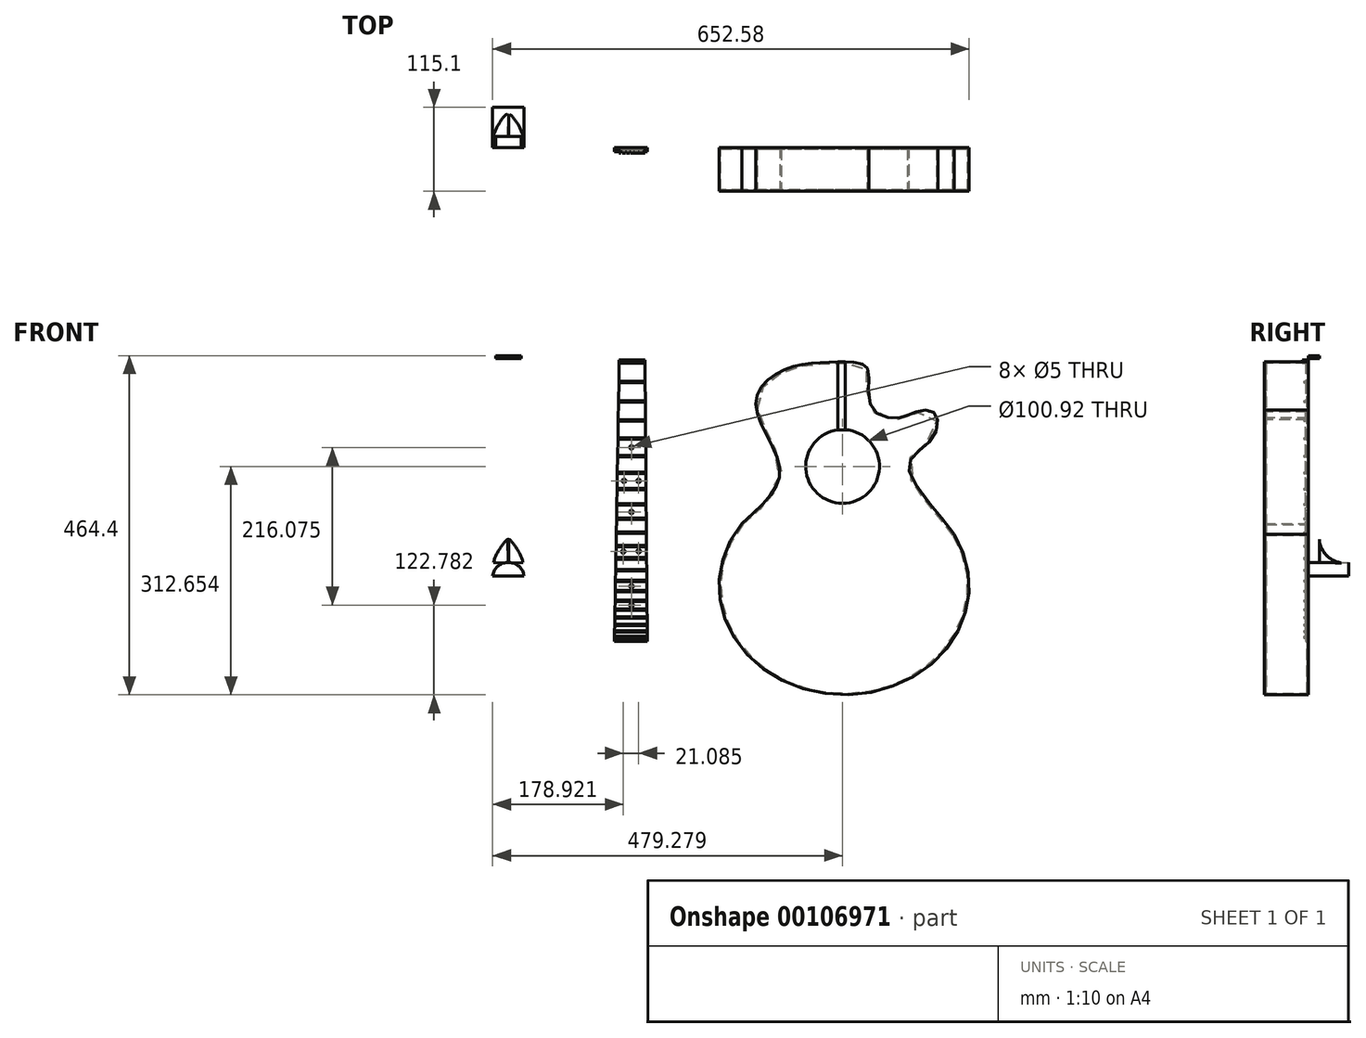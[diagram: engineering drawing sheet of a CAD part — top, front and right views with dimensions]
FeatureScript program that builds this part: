
annotation { "Feature Type Name" : "Feature", "Feature Type Description" : "" }
export const myFeature = defineFeature(function(context is Context, id is Id, definition is map)
    precondition{}
    {
        {
            var Q0;
            Q0=qCreatedBy(makeId("Front.planeOp"),FACE);
            var sketch = newSketch(context, id + "F0", { "sketchPlane" : qUnion([Q0])});
            skLineSegment(sketch, "E0.bottom", {"start": v(-21.8, 190.75) * mm, "end": v(23.4, 190.75) * mm});
            skLineSegment(sketch, "E0.top", {"start": v(-23.4, -190.75) * mm, "end": v(21.6, -190.75) * mm});
            skPoint(sketch, "E0.middle", {"position": v(0, 0) * mm});
            skLineSegment(sketch, "E1", {"start": v(-21.9, 165.75) * mm, "end": v(23.28, 165.75) * mm});
            skLineSegment(sketch, "E2", {"start": v(-21.91, 163.75) * mm, "end": v(23.27, 163.75) * mm});
            skLineSegment(sketch, "E3", {"start": v(-22.02, 139.25) * mm, "end": v(23.16, 139.25) * mm});
            skLineSegment(sketch, "E4", {"start": v(23.15, 137.25) * mm, "end": v(-22.02, 137.25) * mm});
            skLineSegment(sketch, "E5", {"start": v(-22.13, 113.25) * mm, "end": v(23.03, 113.25) * mm});
            skLineSegment(sketch, "E6", {"start": v(23.02, 111.25) * mm, "end": v(-22.13, 111.25) * mm});
            skLineSegment(sketch, "E7", {"start": v(-22.23, 88.25) * mm, "end": v(22.92, 88.25) * mm});
            skLineSegment(sketch, "E8", {"start": v(22.9, 86.25) * mm, "end": v(-22.24, 86.25) * mm});
            skLineSegment(sketch, "E9", {"start": v(-22.33, 64.25) * mm, "end": v(22.8, 64.25) * mm});
            skLineSegment(sketch, "E10", {"start": v(22.8, 62.25) * mm, "end": v(-22.34, 62.25) * mm});
            skLineSegment(sketch, "E11", {"start": v(-22.43, 41.25) * mm, "end": v(22.7, 41.25) * mm});
            skLineSegment(sketch, "E12", {"start": v(22.69, 39.25) * mm, "end": v(-22.44, 39.25) * mm});
            skLineSegment(sketch, "E13", {"start": v(-22.52, 19.25) * mm, "end": v(22.6, 19.25) * mm});
            skLineSegment(sketch, "E14", {"start": v(22.58, 17.25) * mm, "end": v(-22.53, 17.25) * mm});
            skLineSegment(sketch, "E15", {"start": v(-22.6, -1.75) * mm, "end": v(22.5, -1.75) * mm});
            skLineSegment(sketch, "E16", {"start": v(22.48, -3.75) * mm, "end": v(-22.62, -3.75) * mm});
            skLineSegment(sketch, "E17", {"start": v(-22.7, -21.75) * mm, "end": v(22.4, -21.75) * mm});
            skLineSegment(sketch, "E18", {"start": v(22.39, -23.75) * mm, "end": v(-22.7, -23.75) * mm});
            skLineSegment(sketch, "E19", {"start": v(-22.77, -40.75) * mm, "end": v(22.3, -40.75) * mm});
            skLineSegment(sketch, "E20", {"start": v(22.3, -42.75) * mm, "end": v(-22.78, -42.75) * mm});
            skLineSegment(sketch, "E21", {"start": v(-22.85, -58.75) * mm, "end": v(22.22, -58.75) * mm});
            skLineSegment(sketch, "E22", {"start": v(22.21, -60.75) * mm, "end": v(-22.85, -60.75) * mm});
            skLineSegment(sketch, "E23", {"start": v(-22.92, -75.75) * mm, "end": v(22.14, -75.75) * mm});
            skLineSegment(sketch, "E24", {"start": v(22.13, -77.75) * mm, "end": v(-22.93, -77.75) * mm});
            skLineSegment(sketch, "E25", {"start": v(-22.98, -91.75) * mm, "end": v(22.07, -91.75) * mm});
            skLineSegment(sketch, "E26", {"start": v(22.06, -93.75) * mm, "end": v(-23, -93.75) * mm});
            skLineSegment(sketch, "E27", {"start": v(-23.05, -106.75) * mm, "end": v(22, -106.75) * mm});
            skLineSegment(sketch, "E28", {"start": v(21.99, -108.75) * mm, "end": v(-23.06, -108.75) * mm});
            skLineSegment(sketch, "E29", {"start": v(-23.1, -120.75) * mm, "end": v(21.93, -120.75) * mm});
            skLineSegment(sketch, "E30", {"start": v(21.92, -122.75) * mm, "end": v(-23.11, -122.75) * mm});
            skLineSegment(sketch, "E31", {"start": v(-23.16, -133.75) * mm, "end": v(21.87, -133.75) * mm});
            skLineSegment(sketch, "E32", {"start": v(21.86, -135.75) * mm, "end": v(-23.17, -135.75) * mm});
            skLineSegment(sketch, "E33", {"start": v(-23.21, -145.75) * mm, "end": v(21.81, -145.75) * mm});
            skLineSegment(sketch, "E34", {"start": v(21.8, -147.75) * mm, "end": v(-23.22, -147.75) * mm});
            skLineSegment(sketch, "E35", {"start": v(-23.26, -156.75) * mm, "end": v(21.76, -156.75) * mm});
            skLineSegment(sketch, "E36", {"start": v(21.75, -158.75) * mm, "end": v(-23.27, -158.75) * mm});
            skLineSegment(sketch, "E37", {"start": v(-23.3, -166.75) * mm, "end": v(21.71, -166.75) * mm});
            skLineSegment(sketch, "E38", {"start": v(21.7, -168.75) * mm, "end": v(-23.3, -168.75) * mm});
            skLineSegment(sketch, "E39", {"start": v(-23.34, -175.75) * mm, "end": v(21.67, -175.75) * mm});
            skLineSegment(sketch, "E40", {"start": v(21.66, -177.75) * mm, "end": v(-23.35, -177.75) * mm});
            skLineSegment(sketch, "E41", {"start": v(-23.37, -183.75) * mm, "end": v(21.63, -183.75) * mm});
            skLineSegment(sketch, "E42", {"start": v(21.62, -185.75) * mm, "end": v(-23.38, -185.75) * mm});
            skLineSegment(sketch, "E43", {"start": v(-23.4, -190.75) * mm, "end": v(-21.8, 190.75) * mm});
            skLineSegment(sketch, "E44", {"start": v(23.4, 190.75) * mm, "end": v(21.6, -190.75) * mm});
            skPoint(sketch, "E45.orphan", {"position": v(23.4, 190.75) * mm});
            skPoint(sketch, "E46.orphan", {"position": v(-22.5, -23.75) * mm});
            skPoint(sketch, "E47.orphan", {"position": v(-22.5, -21.75) * mm});
            skPoint(sketch, "E48.orphan", {"position": v(-21.6, 190.75) * mm});
            skLineSegment(sketch, "E49.top", {"start": v(-21.8, 194.75) * mm, "end": v(23.4, 194.75) * mm});
            skLineSegment(sketch, "E49.left", {"start": v(-21.8, 190.75) * mm, "end": v(-21.8, 194.75) * mm});
            skLineSegment(sketch, "E49.right", {"start": v(23.4, 190.75) * mm, "end": v(23.4, 194.75) * mm});
            skLineSegment(sketch, "E50", {"start": v(-14.3, 194.75) * mm, "end": v(-14.3, 190.75) * mm});
            skLineSegment(sketch, "E51", {"start": v(-12.8, 194.75) * mm, "end": v(-12.8, 190.75) * mm});
            skLineSegment(sketch, "E52", {"start": v(-8.3, 194.75) * mm, "end": v(-8.3, 190.75) * mm});
            skLineSegment(sketch, "E53", {"start": v(-7, 194.75) * mm, "end": v(-7, 190.75) * mm});
            skLineSegment(sketch, "E54", {"start": v(-2.5, 194.75) * mm, "end": v(-2.5, 190.75) * mm});
            skLineSegment(sketch, "E55", {"start": v(3.8, 194.75) * mm, "end": v(3.8, 190.75) * mm});
            skLineSegment(sketch, "E56", {"start": v(-1.5, 194.75) * mm, "end": v(-1.5, 190.75) * mm});
            skLineSegment(sketch, "E57", {"start": v(3, 194.75) * mm, "end": v(3, 190.75) * mm});
            skLineSegment(sketch, "E58", {"start": v(9.3, 194.75) * mm, "end": v(9.3, 190.75) * mm});
            skLineSegment(sketch, "E59", {"start": v(9.9, 194.75) * mm, "end": v(9.88, 190.75) * mm});
            skLineSegment(sketch, "E60", {"start": v(15.4, 194.75) * mm, "end": v(15.4, 190.75) * mm});
            skLineSegment(sketch, "E61", {"start": v(15.9, 194.75) * mm, "end": v(15.9, 190.75) * mm});
            skLineSegment(sketch, "E62", {"start": v(-21.8, 194.75) * mm, "end": v(0.8, 194.75) * mm});
            skCircle(sketch, "E63", {"center": v(0, 75.28) * mm, "radius": 2.5 * mm});
            skCircle(sketch, "E64", {"center": v(-10.14, 29.45) * mm, "radius": 2.5 * mm});
            skCircle(sketch, "E65", {"center": v(9.6, 29.46) * mm, "radius": 2.5 * mm});
            skCircle(sketch, "E66", {"center": v(0, -13.09) * mm, "radius": 2.5 * mm});
            skCircle(sketch, "E67", {"center": v(0, -140.8) * mm, "radius": 2.5 * mm});
            skCircle(sketch, "E68", {"center": v(0, -115) * mm, "radius": 2.5 * mm});
            skCircle(sketch, "E69", {"center": v(-11.24, -67.4) * mm, "radius": 2.5 * mm});
            skCircle(sketch, "E70", {"center": v(9.85, -67.03) * mm, "radius": 2.5 * mm});
            skLineSegment(sketch, "E71", {"start": v(21.6, -190.75) * mm, "end": v(18.4, 190.75) * mm});
            skLineSegment(sketch, "E72", {"start": v(-16.8, 190.75) * mm, "end": v(-23.4, -190.75) * mm});
            skLineSegment(sketch, "E73", {"start": v(-16.8, 190.75) * mm, "end": v(-16.8, 194.75) * mm});
            skLineSegment(sketch, "E74", {"start": v(18.4, 190.75) * mm, "end": v(18.4, 194.75) * mm});
            skSolve(sketch);
        }
        {
            var Q0;
            {var subQ10=sQuery(id+"F0.wireOp",EDGE,"E72");var subQ12=sQuery(id+"F0.wireOp",EDGE,"E1");var subQ13=makeQuery(id+"F0.imprint","INTERSECT",VERTEX,{"derivedFrom":[subQ12,subQ10]});Q0=makeQuery(id+"F0.imprint","IMPRINT",FACE,{"disambiguationData":[TD([[makeQuery(id+"F0.imprint","IMPRINT",EDGE,{"disambiguationData":[TD([[subQ13,-1.0]])],"derivedFrom":subQ12}),1.0]])]});}
            var Q1;
            {var subQ0=sQuery(id+"F0.wireOp",EDGE,"E72");var subQ1=sQuery(id+"F0.wireOp",EDGE,"E2");var subQ2=makeQuery(id+"F0.imprint","INTERSECT",VERTEX,{"derivedFrom":[subQ1,subQ0]});Q1=makeQuery(id+"F0.imprint","IMPRINT",FACE,{"disambiguationData":[TD([[makeQuery(id+"F0.imprint","IMPRINT",EDGE,{"disambiguationData":[TD([[subQ2,-1.0]])],"derivedFrom":subQ1}),-1.0]])]});}
            var Q2;
            {var subQ0=sQuery(id+"F0.wireOp",EDGE,"E71");var subQ1=sQuery(id+"F0.wireOp",EDGE,"E4");var subQ2=makeQuery(id+"F0.imprint","INTERSECT",VERTEX,{"derivedFrom":[subQ1,subQ0]});Q2=makeQuery(id+"F0.imprint","IMPRINT",FACE,{"disambiguationData":[TD([[makeQuery(id+"F0.imprint","IMPRINT",EDGE,{"disambiguationData":[TD([[subQ2,-1.0]])],"derivedFrom":subQ1}),1.0]])]});}
            var Q3;
            {var subQ0=sQuery(id+"F0.wireOp",EDGE,"E71");var subQ1=sQuery(id+"F0.wireOp",EDGE,"E6");var subQ2=makeQuery(id+"F0.imprint","INTERSECT",VERTEX,{"derivedFrom":[subQ1,subQ0]});Q3=makeQuery(id+"F0.imprint","IMPRINT",FACE,{"disambiguationData":[TD([[makeQuery(id+"F0.imprint","IMPRINT",EDGE,{"disambiguationData":[TD([[subQ2,-1.0]])],"derivedFrom":subQ1}),1.0]])]});}
            var Q4;
            Q4=makeQuery(id+"F0.imprint","IMPRINT",FACE,{"disambiguationData":[TD([[makeQuery(id+"F0.imprint","IMPRINT",EDGE,{"derivedFrom":sQuery(id+"F0.wireOp",EDGE,"E63")}),-1.0]])]});
            var Q5;
            {var subQ0=sQuery(id+"F0.wireOp",EDGE,"E71");var subQ1=sQuery(id+"F0.wireOp",EDGE,"E10");var subQ2=makeQuery(id+"F0.imprint","INTERSECT",VERTEX,{"derivedFrom":[subQ1,subQ0]});Q5=makeQuery(id+"F0.imprint","IMPRINT",FACE,{"disambiguationData":[TD([[makeQuery(id+"F0.imprint","IMPRINT",EDGE,{"disambiguationData":[TD([[subQ2,-1.0]])],"derivedFrom":subQ1}),1.0]])]});}
            var Q6;
            Q6=makeQuery(id+"F0.imprint","IMPRINT",FACE,{"disambiguationData":[TD([[makeQuery(id+"F0.imprint","IMPRINT",EDGE,{"derivedFrom":sQuery(id+"F0.wireOp",EDGE,"E64")}),-1.0]])]});
            var Q7;
            {var subQ0=sQuery(id+"F0.wireOp",EDGE,"E71");var subQ1=sQuery(id+"F0.wireOp",EDGE,"E14");var subQ2=makeQuery(id+"F0.imprint","INTERSECT",VERTEX,{"derivedFrom":[subQ1,subQ0]});Q7=makeQuery(id+"F0.imprint","IMPRINT",FACE,{"disambiguationData":[TD([[makeQuery(id+"F0.imprint","IMPRINT",EDGE,{"disambiguationData":[TD([[subQ2,-1.0]])],"derivedFrom":subQ1}),1.0]])]});}
            var Q8;
            Q8=makeQuery(id+"F0.imprint","IMPRINT",FACE,{"disambiguationData":[TD([[makeQuery(id+"F0.imprint","IMPRINT",EDGE,{"derivedFrom":sQuery(id+"F0.wireOp",EDGE,"E66")}),-1.0]])]});
            var Q9;
            {var subQ0=sQuery(id+"F0.wireOp",EDGE,"E71");var subQ1=sQuery(id+"F0.wireOp",EDGE,"E18");var subQ2=makeQuery(id+"F0.imprint","INTERSECT",VERTEX,{"derivedFrom":[subQ1,subQ0]});Q9=makeQuery(id+"F0.imprint","IMPRINT",FACE,{"disambiguationData":[TD([[makeQuery(id+"F0.imprint","IMPRINT",EDGE,{"disambiguationData":[TD([[subQ2,-1.0]])],"derivedFrom":subQ1}),1.0]])]});}
            var Q10;
            {var subQ0=sQuery(id+"F0.wireOp",EDGE,"E71");var subQ1=sQuery(id+"F0.wireOp",EDGE,"E20");var subQ2=makeQuery(id+"F0.imprint","INTERSECT",VERTEX,{"derivedFrom":[subQ1,subQ0]});Q10=makeQuery(id+"F0.imprint","IMPRINT",FACE,{"disambiguationData":[TD([[makeQuery(id+"F0.imprint","IMPRINT",EDGE,{"disambiguationData":[TD([[subQ2,-1.0]])],"derivedFrom":subQ1}),1.0]])]});}
            var Q11;
            Q11=makeQuery(id+"F0.imprint","IMPRINT",FACE,{"disambiguationData":[TD([[makeQuery(id+"F0.imprint","IMPRINT",EDGE,{"derivedFrom":sQuery(id+"F0.wireOp",EDGE,"E69")}),-1.0]])]});
            var Q12;
            {var subQ0=sQuery(id+"F0.wireOp",EDGE,"E71");var subQ1=sQuery(id+"F0.wireOp",EDGE,"E24");var subQ2=makeQuery(id+"F0.imprint","INTERSECT",VERTEX,{"derivedFrom":[subQ1,subQ0]});Q12=makeQuery(id+"F0.imprint","IMPRINT",FACE,{"disambiguationData":[TD([[makeQuery(id+"F0.imprint","IMPRINT",EDGE,{"disambiguationData":[TD([[subQ2,-1.0]])],"derivedFrom":subQ1}),1.0]])]});}
            var Q13;
            {var subQ0=sQuery(id+"F0.wireOp",EDGE,"E71");var subQ1=sQuery(id+"F0.wireOp",EDGE,"E26");var subQ2=makeQuery(id+"F0.imprint","INTERSECT",VERTEX,{"derivedFrom":[subQ1,subQ0]});Q13=makeQuery(id+"F0.imprint","IMPRINT",FACE,{"disambiguationData":[TD([[makeQuery(id+"F0.imprint","IMPRINT",EDGE,{"disambiguationData":[TD([[subQ2,-1.0]])],"derivedFrom":subQ1}),1.0]])]});}
            var Q14;
            Q14=makeQuery(id+"F0.imprint","IMPRINT",FACE,{"disambiguationData":[TD([[makeQuery(id+"F0.imprint","IMPRINT",EDGE,{"derivedFrom":sQuery(id+"F0.wireOp",EDGE,"E68")}),-1.0]])]});
            var Q15;
            {var subQ0=sQuery(id+"F0.wireOp",EDGE,"E71");var subQ1=sQuery(id+"F0.wireOp",EDGE,"E30");var subQ2=makeQuery(id+"F0.imprint","INTERSECT",VERTEX,{"derivedFrom":[subQ1,subQ0]});Q15=makeQuery(id+"F0.imprint","IMPRINT",FACE,{"disambiguationData":[TD([[makeQuery(id+"F0.imprint","IMPRINT",EDGE,{"disambiguationData":[TD([[subQ2,-1.0]])],"derivedFrom":subQ1}),1.0]])]});}
            var Q16;
            Q16=makeQuery(id+"F0.imprint","IMPRINT",FACE,{"disambiguationData":[TD([[makeQuery(id+"F0.imprint","IMPRINT",EDGE,{"derivedFrom":sQuery(id+"F0.wireOp",EDGE,"E67")}),-1.0]])]});
            var Q17;
            {var subQ0=sQuery(id+"F0.wireOp",EDGE,"E71");var subQ1=sQuery(id+"F0.wireOp",EDGE,"E34");var subQ2=makeQuery(id+"F0.imprint","INTERSECT",VERTEX,{"derivedFrom":[subQ1,subQ0]});Q17=makeQuery(id+"F0.imprint","IMPRINT",FACE,{"disambiguationData":[TD([[makeQuery(id+"F0.imprint","IMPRINT",EDGE,{"disambiguationData":[TD([[subQ2,-1.0]])],"derivedFrom":subQ1}),1.0]])]});}
            var Q18;
            {var subQ0=sQuery(id+"F0.wireOp",EDGE,"E71");var subQ1=sQuery(id+"F0.wireOp",EDGE,"E36");var subQ2=makeQuery(id+"F0.imprint","INTERSECT",VERTEX,{"derivedFrom":[subQ1,subQ0]});Q18=makeQuery(id+"F0.imprint","IMPRINT",FACE,{"disambiguationData":[TD([[makeQuery(id+"F0.imprint","IMPRINT",EDGE,{"disambiguationData":[TD([[subQ2,-1.0]])],"derivedFrom":subQ1}),1.0]])]});}
            var Q19;
            {var subQ0=sQuery(id+"F0.wireOp",EDGE,"E71");var subQ1=sQuery(id+"F0.wireOp",EDGE,"E38");var subQ2=makeQuery(id+"F0.imprint","INTERSECT",VERTEX,{"derivedFrom":[subQ1,subQ0]});Q19=makeQuery(id+"F0.imprint","IMPRINT",FACE,{"disambiguationData":[TD([[makeQuery(id+"F0.imprint","IMPRINT",EDGE,{"disambiguationData":[TD([[subQ2,-1.0]])],"derivedFrom":subQ1}),1.0]])]});}
            var Q20;
            {var subQ0=sQuery(id+"F0.wireOp",EDGE,"E71");var subQ1=sQuery(id+"F0.wireOp",EDGE,"E40");var subQ2=makeQuery(id+"F0.imprint","INTERSECT",VERTEX,{"derivedFrom":[subQ1,subQ0]});Q20=makeQuery(id+"F0.imprint","IMPRINT",FACE,{"disambiguationData":[TD([[makeQuery(id+"F0.imprint","IMPRINT",EDGE,{"disambiguationData":[TD([[subQ2,-1.0]])],"derivedFrom":subQ1}),1.0]])]});}
            var Q21;
            {var subQ0=sQuery(id+"F0.wireOp",EDGE,"E0.top");Q21=makeQuery(id+"F0.imprint","IMPRINT",FACE,{"disambiguationData":[TD([[makeQuery(id+"F0.imprint","IMPRINT",EDGE,{"derivedFrom":subQ0}),1.0]])]});}
            extrude(context, id + "F1", {"entities" : qUnion([Q0, Q1, Q2, Q3, Q4, Q5, Q6, Q7, Q8, Q9, Q10, Q11, Q12, Q13, Q14, Q15, Q16, Q17, Q18, Q19, Q20, Q21]), "depth" : 4 * mm});
        }
        {
            var Q0;
            {var subQ0=sQuery(id+"F0.wireOp",EDGE,"E72");var subQ1=sQuery(id+"F0.wireOp",EDGE,"E1");var subQ2=makeQuery(id+"F0.imprint","INTERSECT",VERTEX,{"derivedFrom":[subQ1,subQ0]});Q0=makeQuery(id+"F0.imprint","IMPRINT",FACE,{"disambiguationData":[TD([[makeQuery(id+"F0.imprint","IMPRINT",EDGE,{"disambiguationData":[TD([[subQ2,-1.0]])],"derivedFrom":subQ1}),-1.0]])]});}
            var Q1;
            {var subQ0=sQuery(id+"F0.wireOp",EDGE,"E72");var subQ1=sQuery(id+"F0.wireOp",EDGE,"E3");var subQ2=makeQuery(id+"F0.imprint","INTERSECT",VERTEX,{"derivedFrom":[subQ1,subQ0]});Q1=makeQuery(id+"F0.imprint","IMPRINT",FACE,{"disambiguationData":[TD([[makeQuery(id+"F0.imprint","IMPRINT",EDGE,{"disambiguationData":[TD([[subQ2,-1.0]])],"derivedFrom":subQ1}),-1.0]])]});}
            var Q2;
            {var subQ0=sQuery(id+"F0.wireOp",EDGE,"E72");var subQ1=sQuery(id+"F0.wireOp",EDGE,"E5");var subQ2=makeQuery(id+"F0.imprint","INTERSECT",VERTEX,{"derivedFrom":[subQ1,subQ0]});Q2=makeQuery(id+"F0.imprint","IMPRINT",FACE,{"disambiguationData":[TD([[makeQuery(id+"F0.imprint","IMPRINT",EDGE,{"disambiguationData":[TD([[subQ2,-1.0]])],"derivedFrom":subQ1}),-1.0]])]});}
            var Q3;
            {var subQ0=sQuery(id+"F0.wireOp",EDGE,"E72");var subQ1=sQuery(id+"F0.wireOp",EDGE,"E7");var subQ2=makeQuery(id+"F0.imprint","INTERSECT",VERTEX,{"derivedFrom":[subQ1,subQ0]});Q3=makeQuery(id+"F0.imprint","IMPRINT",FACE,{"disambiguationData":[TD([[makeQuery(id+"F0.imprint","IMPRINT",EDGE,{"disambiguationData":[TD([[subQ2,-1.0]])],"derivedFrom":subQ1}),-1.0]])]});}
            var Q4;
            {var subQ0=sQuery(id+"F0.wireOp",EDGE,"E72");var subQ1=sQuery(id+"F0.wireOp",EDGE,"E9");var subQ2=makeQuery(id+"F0.imprint","INTERSECT",VERTEX,{"derivedFrom":[subQ1,subQ0]});Q4=makeQuery(id+"F0.imprint","IMPRINT",FACE,{"disambiguationData":[TD([[makeQuery(id+"F0.imprint","IMPRINT",EDGE,{"disambiguationData":[TD([[subQ2,-1.0]])],"derivedFrom":subQ1}),-1.0]])]});}
            var Q5;
            {var subQ0=sQuery(id+"F0.wireOp",EDGE,"E72");var subQ1=sQuery(id+"F0.wireOp",EDGE,"E11");var subQ2=makeQuery(id+"F0.imprint","INTERSECT",VERTEX,{"derivedFrom":[subQ1,subQ0]});Q5=makeQuery(id+"F0.imprint","IMPRINT",FACE,{"disambiguationData":[TD([[makeQuery(id+"F0.imprint","IMPRINT",EDGE,{"disambiguationData":[TD([[subQ2,-1.0]])],"derivedFrom":subQ1}),-1.0]])]});}
            var Q6;
            {var subQ0=sQuery(id+"F0.wireOp",EDGE,"E72");var subQ1=sQuery(id+"F0.wireOp",EDGE,"E13");var subQ2=makeQuery(id+"F0.imprint","INTERSECT",VERTEX,{"derivedFrom":[subQ1,subQ0]});Q6=makeQuery(id+"F0.imprint","IMPRINT",FACE,{"disambiguationData":[TD([[makeQuery(id+"F0.imprint","IMPRINT",EDGE,{"disambiguationData":[TD([[subQ2,-1.0]])],"derivedFrom":subQ1}),-1.0]])]});}
            var Q7;
            {var subQ0=sQuery(id+"F0.wireOp",EDGE,"E72");var subQ1=sQuery(id+"F0.wireOp",EDGE,"E15");var subQ2=makeQuery(id+"F0.imprint","INTERSECT",VERTEX,{"derivedFrom":[subQ1,subQ0]});Q7=makeQuery(id+"F0.imprint","IMPRINT",FACE,{"disambiguationData":[TD([[makeQuery(id+"F0.imprint","IMPRINT",EDGE,{"disambiguationData":[TD([[subQ2,-1.0]])],"derivedFrom":subQ1}),-1.0]])]});}
            var Q8;
            {var subQ0=sQuery(id+"F0.wireOp",EDGE,"E72");var subQ1=sQuery(id+"F0.wireOp",EDGE,"E17");var subQ2=makeQuery(id+"F0.imprint","INTERSECT",VERTEX,{"derivedFrom":[subQ1,subQ0]});Q8=makeQuery(id+"F0.imprint","IMPRINT",FACE,{"disambiguationData":[TD([[makeQuery(id+"F0.imprint","IMPRINT",EDGE,{"disambiguationData":[TD([[subQ2,-1.0]])],"derivedFrom":subQ1}),-1.0]])]});}
            var Q9;
            {var subQ0=sQuery(id+"F0.wireOp",EDGE,"E72");var subQ1=sQuery(id+"F0.wireOp",EDGE,"E19");var subQ2=makeQuery(id+"F0.imprint","INTERSECT",VERTEX,{"derivedFrom":[subQ1,subQ0]});Q9=makeQuery(id+"F0.imprint","IMPRINT",FACE,{"disambiguationData":[TD([[makeQuery(id+"F0.imprint","IMPRINT",EDGE,{"disambiguationData":[TD([[subQ2,-1.0]])],"derivedFrom":subQ1}),-1.0]])]});}
            var Q10;
            {var subQ0=sQuery(id+"F0.wireOp",EDGE,"E72");var subQ1=sQuery(id+"F0.wireOp",EDGE,"E21");var subQ2=makeQuery(id+"F0.imprint","INTERSECT",VERTEX,{"derivedFrom":[subQ1,subQ0]});Q10=makeQuery(id+"F0.imprint","IMPRINT",FACE,{"disambiguationData":[TD([[makeQuery(id+"F0.imprint","IMPRINT",EDGE,{"disambiguationData":[TD([[subQ2,-1.0]])],"derivedFrom":subQ1}),-1.0]])]});}
            var Q11;
            {var subQ0=sQuery(id+"F0.wireOp",EDGE,"E72");var subQ1=sQuery(id+"F0.wireOp",EDGE,"E23");var subQ2=makeQuery(id+"F0.imprint","INTERSECT",VERTEX,{"derivedFrom":[subQ1,subQ0]});Q11=makeQuery(id+"F0.imprint","IMPRINT",FACE,{"disambiguationData":[TD([[makeQuery(id+"F0.imprint","IMPRINT",EDGE,{"disambiguationData":[TD([[subQ2,-1.0]])],"derivedFrom":subQ1}),-1.0]])]});}
            var Q12;
            {var subQ0=sQuery(id+"F0.wireOp",EDGE,"E72");var subQ1=sQuery(id+"F0.wireOp",EDGE,"E25");var subQ2=makeQuery(id+"F0.imprint","INTERSECT",VERTEX,{"derivedFrom":[subQ1,subQ0]});Q12=makeQuery(id+"F0.imprint","IMPRINT",FACE,{"disambiguationData":[TD([[makeQuery(id+"F0.imprint","IMPRINT",EDGE,{"disambiguationData":[TD([[subQ2,-1.0]])],"derivedFrom":subQ1}),-1.0]])]});}
            var Q13;
            {var subQ0=sQuery(id+"F0.wireOp",EDGE,"E72");var subQ1=sQuery(id+"F0.wireOp",EDGE,"E27");var subQ2=makeQuery(id+"F0.imprint","INTERSECT",VERTEX,{"derivedFrom":[subQ1,subQ0]});Q13=makeQuery(id+"F0.imprint","IMPRINT",FACE,{"disambiguationData":[TD([[makeQuery(id+"F0.imprint","IMPRINT",EDGE,{"disambiguationData":[TD([[subQ2,-1.0]])],"derivedFrom":subQ1}),-1.0]])]});}
            var Q14;
            {var subQ0=sQuery(id+"F0.wireOp",EDGE,"E72");var subQ1=sQuery(id+"F0.wireOp",EDGE,"E29");var subQ2=makeQuery(id+"F0.imprint","INTERSECT",VERTEX,{"derivedFrom":[subQ1,subQ0]});Q14=makeQuery(id+"F0.imprint","IMPRINT",FACE,{"disambiguationData":[TD([[makeQuery(id+"F0.imprint","IMPRINT",EDGE,{"disambiguationData":[TD([[subQ2,-1.0]])],"derivedFrom":subQ1}),-1.0]])]});}
            var Q15;
            {var subQ0=sQuery(id+"F0.wireOp",EDGE,"E72");var subQ1=sQuery(id+"F0.wireOp",EDGE,"E31");var subQ2=makeQuery(id+"F0.imprint","INTERSECT",VERTEX,{"derivedFrom":[subQ1,subQ0]});Q15=makeQuery(id+"F0.imprint","IMPRINT",FACE,{"disambiguationData":[TD([[makeQuery(id+"F0.imprint","IMPRINT",EDGE,{"disambiguationData":[TD([[subQ2,-1.0]])],"derivedFrom":subQ1}),-1.0]])]});}
            var Q16;
            {var subQ0=sQuery(id+"F0.wireOp",EDGE,"E72");var subQ1=sQuery(id+"F0.wireOp",EDGE,"E33");var subQ2=makeQuery(id+"F0.imprint","INTERSECT",VERTEX,{"derivedFrom":[subQ1,subQ0]});Q16=makeQuery(id+"F0.imprint","IMPRINT",FACE,{"disambiguationData":[TD([[makeQuery(id+"F0.imprint","IMPRINT",EDGE,{"disambiguationData":[TD([[subQ2,-1.0]])],"derivedFrom":subQ1}),-1.0]])]});}
            var Q17;
            {var subQ0=sQuery(id+"F0.wireOp",EDGE,"E72");var subQ1=sQuery(id+"F0.wireOp",EDGE,"E35");var subQ2=makeQuery(id+"F0.imprint","INTERSECT",VERTEX,{"derivedFrom":[subQ1,subQ0]});Q17=makeQuery(id+"F0.imprint","IMPRINT",FACE,{"disambiguationData":[TD([[makeQuery(id+"F0.imprint","IMPRINT",EDGE,{"disambiguationData":[TD([[subQ2,-1.0]])],"derivedFrom":subQ1}),-1.0]])]});}
            var Q18;
            {var subQ0=sQuery(id+"F0.wireOp",EDGE,"E72");var subQ1=sQuery(id+"F0.wireOp",EDGE,"E37");var subQ2=makeQuery(id+"F0.imprint","INTERSECT",VERTEX,{"derivedFrom":[subQ1,subQ0]});Q18=makeQuery(id+"F0.imprint","IMPRINT",FACE,{"disambiguationData":[TD([[makeQuery(id+"F0.imprint","IMPRINT",EDGE,{"disambiguationData":[TD([[subQ2,-1.0]])],"derivedFrom":subQ1}),-1.0]])]});}
            var Q19;
            {var subQ0=sQuery(id+"F0.wireOp",EDGE,"E72");var subQ1=sQuery(id+"F0.wireOp",EDGE,"E39");var subQ2=makeQuery(id+"F0.imprint","INTERSECT",VERTEX,{"derivedFrom":[subQ1,subQ0]});Q19=makeQuery(id+"F0.imprint","IMPRINT",FACE,{"disambiguationData":[TD([[makeQuery(id+"F0.imprint","IMPRINT",EDGE,{"disambiguationData":[TD([[subQ2,-1.0]])],"derivedFrom":subQ1}),-1.0]])]});}
            var Q20;
            {var subQ0=sQuery(id+"F0.wireOp",EDGE,"E72");var subQ1=sQuery(id+"F0.wireOp",EDGE,"E41");var subQ2=makeQuery(id+"F0.imprint","INTERSECT",VERTEX,{"derivedFrom":[subQ1,subQ0]});Q20=makeQuery(id+"F0.imprint","IMPRINT",FACE,{"disambiguationData":[TD([[makeQuery(id+"F0.imprint","IMPRINT",EDGE,{"disambiguationData":[TD([[subQ2,-1.0]])],"derivedFrom":subQ1}),-1.0]])]});}
            extrude(context, id + "F2", {"entities" : qUnion([Q0, Q1, Q2, Q3, Q4, Q5, Q6, Q7, Q8, Q9, Q10, Q11, Q12, Q13, Q14, Q15, Q16, Q17, Q18, Q19, Q20]), "depth" : 6 * mm});
        }
        {
            var Q0;
            {var subQ0=sQuery(id+"F0.wireOp",EDGE,"E50");Q0=makeQuery(id+"F0.imprint","IMPRINT",FACE,{"disambiguationData":[TD([[makeQuery(id+"F0.imprint","IMPRINT",EDGE,{"derivedFrom":subQ0}),1.0]])]});}
            var Q1;
            {var subQ0=sQuery(id+"F0.wireOp",EDGE,"E52");Q1=makeQuery(id+"F0.imprint","IMPRINT",FACE,{"disambiguationData":[TD([[makeQuery(id+"F0.imprint","IMPRINT",EDGE,{"derivedFrom":subQ0}),1.0]])]});}
            var Q2;
            {var subQ0=sQuery(id+"F0.wireOp",EDGE,"E54");Q2=makeQuery(id+"F0.imprint","IMPRINT",FACE,{"disambiguationData":[TD([[makeQuery(id+"F0.imprint","IMPRINT",EDGE,{"derivedFrom":subQ0}),1.0]])]});}
            var Q3;
            {var subQ0=sQuery(id+"F0.wireOp",EDGE,"E55");Q3=makeQuery(id+"F0.imprint","IMPRINT",FACE,{"disambiguationData":[TD([[makeQuery(id+"F0.imprint","IMPRINT",EDGE,{"derivedFrom":subQ0}),-1.0]])]});}
            var Q4;
            {var subQ0=sQuery(id+"F0.wireOp",EDGE,"E58");Q4=makeQuery(id+"F0.imprint","IMPRINT",FACE,{"disambiguationData":[TD([[makeQuery(id+"F0.imprint","IMPRINT",EDGE,{"derivedFrom":subQ0}),1.0]])]});}
            var Q5;
            {var subQ0=sQuery(id+"F0.wireOp",EDGE,"E60");Q5=makeQuery(id+"F0.imprint","IMPRINT",FACE,{"disambiguationData":[TD([[makeQuery(id+"F0.imprint","IMPRINT",EDGE,{"derivedFrom":subQ0}),1.0]])]});}
            extrude(context, id + "F3", {"entities" : qUnion([Q0, Q1, Q2, Q3, Q4, Q5]), "operationType" : NewBodyOperationType.ADD, "depth" : 6 * mm});
        }
        {
            var Q0;
            {var subQ0=sQuery(id+"F0.wireOp",EDGE,"E50");Q0=makeQuery(id+"F0.imprint","IMPRINT",FACE,{"disambiguationData":[TD([[makeQuery(id+"F0.imprint","IMPRINT",EDGE,{"derivedFrom":subQ0}),-1.0]])]});}
            var Q1;
            {var subQ0=sQuery(id+"F0.wireOp",EDGE,"E51");Q1=makeQuery(id+"F0.imprint","IMPRINT",FACE,{"disambiguationData":[TD([[makeQuery(id+"F0.imprint","IMPRINT",EDGE,{"derivedFrom":subQ0}),1.0]])]});}
            var Q2;
            {var subQ0=sQuery(id+"F0.wireOp",EDGE,"E53");Q2=makeQuery(id+"F0.imprint","IMPRINT",FACE,{"disambiguationData":[TD([[makeQuery(id+"F0.imprint","IMPRINT",EDGE,{"derivedFrom":subQ0}),1.0]])]});}
            var Q3;
            {var subQ1=sQuery(id+"F0.wireOp",EDGE,"E56");Q3=makeQuery(id+"F0.imprint","IMPRINT",FACE,{"disambiguationData":[TD([[makeQuery(id+"F0.imprint","IMPRINT",EDGE,{"derivedFrom":subQ1}),1.0]])]});}
            var Q4;
            {var subQ0=sQuery(id+"F0.wireOp",EDGE,"E55");Q4=makeQuery(id+"F0.imprint","IMPRINT",FACE,{"disambiguationData":[TD([[makeQuery(id+"F0.imprint","IMPRINT",EDGE,{"derivedFrom":subQ0}),1.0]])]});}
            var Q5;
            {var subQ0=sQuery(id+"F0.wireOp",EDGE,"E59");Q5=makeQuery(id+"F0.imprint","IMPRINT",FACE,{"disambiguationData":[TD([[makeQuery(id+"F0.imprint","IMPRINT",EDGE,{"derivedFrom":subQ0}),1.0]])]});}
            var Q6;
            {var subQ0=sQuery(id+"F0.wireOp",EDGE,"E61");Q6=makeQuery(id+"F0.imprint","IMPRINT",FACE,{"disambiguationData":[TD([[makeQuery(id+"F0.imprint","IMPRINT",EDGE,{"derivedFrom":subQ0}),1.0]])]});}
            extrude(context, id + "F4", {"entities" : qUnion([Q0, Q1, Q2, Q3, Q4, Q5, Q6]), "operationType" : NewBodyOperationType.ADD, "depth" : 8 * mm});
        }
        {
            var Q0;
            Q0=makeQuery(id+"F0.imprint","IMPRINT",FACE,{"disambiguationData":[TD([[makeQuery(id+"F0.imprint","IMPRINT",EDGE,{"derivedFrom":sQuery(id+"F0.wireOp",EDGE,"E63")}),1.0]])]});
            var Q1;
            Q1=makeQuery(id+"F0.imprint","IMPRINT",FACE,{"disambiguationData":[TD([[makeQuery(id+"F0.imprint","IMPRINT",EDGE,{"derivedFrom":sQuery(id+"F0.wireOp",EDGE,"E64")}),1.0]])]});
            var Q2;
            Q2=makeQuery(id+"F0.imprint","IMPRINT",FACE,{"disambiguationData":[TD([[makeQuery(id+"F0.imprint","IMPRINT",EDGE,{"derivedFrom":sQuery(id+"F0.wireOp",EDGE,"E65")}),1.0]])]});
            var Q3;
            Q3=makeQuery(id+"F0.imprint","IMPRINT",FACE,{"disambiguationData":[TD([[makeQuery(id+"F0.imprint","IMPRINT",EDGE,{"derivedFrom":sQuery(id+"F0.wireOp",EDGE,"E66")}),1.0]])]});
            var Q4;
            Q4=makeQuery(id+"F0.imprint","IMPRINT",FACE,{"disambiguationData":[TD([[makeQuery(id+"F0.imprint","IMPRINT",EDGE,{"derivedFrom":sQuery(id+"F0.wireOp",EDGE,"E69")}),1.0]])]});
            var Q5;
            Q5=makeQuery(id+"F0.imprint","IMPRINT",FACE,{"disambiguationData":[TD([[makeQuery(id+"F0.imprint","IMPRINT",EDGE,{"derivedFrom":sQuery(id+"F0.wireOp",EDGE,"E70")}),1.0]])]});
            var Q6;
            Q6=makeQuery(id+"F0.imprint","IMPRINT",FACE,{"disambiguationData":[TD([[makeQuery(id+"F0.imprint","IMPRINT",EDGE,{"derivedFrom":sQuery(id+"F0.wireOp",EDGE,"E68")}),1.0]])]});
            var Q7;
            Q7=makeQuery(id+"F0.imprint","IMPRINT",FACE,{"disambiguationData":[TD([[makeQuery(id+"F0.imprint","IMPRINT",EDGE,{"derivedFrom":sQuery(id+"F0.wireOp",EDGE,"E67")}),1.0]])]});
            extrude(context, id + "F5", {"entities" : qUnion([Q0, Q1, Q2, Q3, Q4, Q5, Q6, Q7]), "depth" : 3.9 * mm});
        }
        {
            var Q0;
            Q0=qCreatedBy(makeId("Front.planeOp"),FACE);
            var sketch = newSketch(context, id + "F6", { "sketchPlane" : qUnion([Q0])});
            skLineSegment(sketch, "E75.bottom", {"start": v(-191.26, 196.82) * mm, "end": v(-146.26, 196.82) * mm});
            skLineSegment(sketch, "E75.left", {"start": v(-191.26, 196.82) * mm, "end": v(-191.26, -100.68) * mm});
            skLineSegment(sketch, "E75.right", {"start": v(-146.26, 196.82) * mm, "end": v(-146.26, -100.68) * mm});
            skLineSegment(sketch, "E76", {"start": v(-190.16, -100.68) * mm, "end": v(-186.26, 196.82) * mm});
            skLineSegment(sketch, "E77", {"start": v(-147.36, -100.68) * mm, "end": v(-151.26, 196.82) * mm});
            skLineSegment(sketch, "E78.bottom", {"start": v(-186.26, 196.82) * mm, "end": v(-151.26, 196.82) * mm});
            skLineSegment(sketch, "E78.top", {"start": v(-186.26, 200.82) * mm, "end": v(-151.26, 200.82) * mm});
            skLineSegment(sketch, "E78.left", {"start": v(-186.26, 196.82) * mm, "end": v(-186.26, 200.82) * mm});
            skLineSegment(sketch, "E78.right", {"start": v(-151.26, 196.82) * mm, "end": v(-151.26, 200.82) * mm});
            skLineSegment(sketch, "E79", {"start": v(-191.26, -100.68) * mm, "end": v(-146.26, -100.68) * mm});
            skLineSegment(sketch, "E80", {"start": v(-191.26, -82.68) * mm, "end": v(-146.26, -82.68) * mm});
            skSolve(sketch);
        }
        {
            var Q0;
            Q0=makeQuery(id+"F6.imprint","IMPRINT",FACE,{"disambiguationData":[TD([[makeQuery(id+"F6.imprint","IMPRINT",EDGE,{"derivedFrom":sQuery(id+"F6.wireOp",EDGE,"E78.top")}),-1.0]])]});
            var Q1;
            {var subQ0=sQuery(id+"F6.wireOp",EDGE,"E78.bottom");var subQ5=sQuery(id+"F6.wireOp",EDGE,"E77");var subQ6=makeQuery(id+"F6.imprint","INTERSECT",VERTEX,{"derivedFrom":[subQ5,subQ0]});Q1=makeQuery(id+"F6.imprint","IMPRINT",FACE,{"disambiguationData":[TD([[makeQuery(id+"F6.imprint","IMPRINT",EDGE,{"disambiguationData":[TD([[subQ6,1.0]])],"derivedFrom":subQ5}),1.0]])]});}
            extrude(context, id + "F7", {"entities" : qUnion([Q0, Q1]), "oppositeDirection" : true, "depth" : 15 * mm});
        }
        {
            var Q0;
            {var subQ0=sQuery(id+"F6.wireOp",EDGE,"E79");var subQ1=sQuery(id+"F6.wireOp",EDGE,"E76");var subQ2=makeQuery(id+"F6.imprint","INTERSECT",VERTEX,{"derivedFrom":[subQ1,subQ0]});Q0=makeQuery(id+"F6.imprint","IMPRINT",FACE,{"disambiguationData":[TD([[makeQuery(id+"F6.imprint","IMPRINT",EDGE,{"disambiguationData":[TD([[subQ2,-1.0]])],"derivedFrom":subQ1}),-1.0]])]});}
            extrude(context, id + "F8", {"entities" : qUnion([Q0]), "operationType" : NewBodyOperationType.ADD, "oppositeDirection" : true, "depth" : 55 * mm});
        }
        {
            var Q0;
            {var subQ0=sQuery(id+"F6.wireOp",EDGE,"E76");Q0=makeQuery(id+"F8.boolean.opBoolean","MERGE",FACE,{"derivedFrom":[makeQuery(id+"F7.opExtrude","SWEPT_FACE",FACE,{"disambiguationData":[OSD([subQ0])]}),makeQuery(id+"F8.opExtrude","SWEPT_FACE",FACE,{"disambiguationData":[OSD([subQ0])]})]});}
            var sketch = newSketch(context, id + "F9", { "sketchPlane" : qUnion([Q0])});
            skArc(sketch, "E81", {"start": v(-45.74, -85.16) * mm, "mid": v(-24.58, -74.64) * mm, "end": v(-15, -53.04) * mm});
            skLineSegment(sketch, "E82", {"start": v(-45.74, -85.16) * mm, "end": v(-15, -85.16) * mm});
            skLineSegment(sketch, "E83", {"start": v(-15, -85.16) * mm, "end": v(-15, -53.04) * mm});
            skSolve(sketch);
        }
        {
            var Q0;
            Q0=makeQuery(id+"F9.imprint","IMPRINT",FACE,{"disambiguationData":[TD([[makeQuery(id+"F9.imprint","IMPRINT",EDGE,{"derivedFrom":sQuery(id+"F9.wireOp",EDGE,"E81")}),-1.0]])]});
            extrude(context, id + "F10", {"entities" : qUnion([Q0]), "oppositeDirection" : true, "depth" : 21.5 * mm});
        }
        {
            var Q0;
            {var subQ0=sQuery(id+"F6.wireOp",EDGE,"E77");Q0=makeQuery(id+"F8.boolean.opBoolean","MERGE",FACE,{"derivedFrom":[makeQuery(id+"F7.opExtrude","SWEPT_FACE",FACE,{"disambiguationData":[OSD([subQ0])]}),makeQuery(id+"F8.opExtrude","SWEPT_FACE",FACE,{"disambiguationData":[OSD([subQ0])]})]});}
            var sketch = newSketch(context, id + "F11", { "sketchPlane" : qUnion([Q0])});
            skArc(sketch, "E84", {"start": v(15, -48.74) * mm, "mid": v(24.44, -70.08) * mm, "end": v(45.2, -80.73) * mm});
            skLineSegment(sketch, "E85", {"start": v(15, -48.74) * mm, "end": v(15, -80.73) * mm});
            skLineSegment(sketch, "E86", {"start": v(15, -80.73) * mm, "end": v(45.2, -80.73) * mm});
            skSolve(sketch);
        }
        {
            var Q0;
            Q0=makeQuery(id+"F11.imprint","IMPRINT",FACE,{"disambiguationData":[TD([[makeQuery(id+"F11.imprint","IMPRINT",EDGE,{"derivedFrom":sQuery(id+"F11.wireOp",EDGE,"E84")}),-1.0]])]});
            extrude(context, id + "F12", {"entities" : qUnion([Q0]), "oppositeDirection" : true, "depth" : 21.5 * mm});
        }
        {
            var Q0;
            Q0=makeQuery(id+"F7.opExtrude","CAP_EDGE",EDGE,{"disambiguationData":[OSD([sQuery(id+"F6.wireOp",EDGE,"E76")])],"isStart":false});
            var Q1;
            Q1=makeQuery(id+"F10.opExtrude","CAP_EDGE",EDGE,{"disambiguationData":[OSD([sQuery(id+"F9.wireOp",EDGE,"E81")])],"isStart":true});
            var Q2;
            Q2=makeQuery(id+"F8.opExtrude","SWEPT_EDGE",EDGE,{"disambiguationData":[OSD([sQuery(id+"F6.wireOp",EDGE,"E76"),sQuery(id+"F6.wireOp",EDGE,"E80")])]});
            var Q3;
            Q3=makeQuery(id+"F8.opExtrude","SWEPT_EDGE",EDGE,{"disambiguationData":[OSD([sQuery(id+"F6.wireOp",EDGE,"E77"),sQuery(id+"F6.wireOp",EDGE,"E80")])]});
            var Q4;
            Q4=makeQuery(id+"F12.opExtrude","CAP_EDGE",EDGE,{"disambiguationData":[OSD([sQuery(id+"F11.wireOp",EDGE,"E84")])],"isStart":true});
            var Q5;
            Q5=makeQuery(id+"F7.opExtrude","CAP_EDGE",EDGE,{"disambiguationData":[OSD([sQuery(id+"F6.wireOp",EDGE,"E77")])],"isStart":false});
            fillet(context, id + "F13", {"entities" : qUnion([Q0, Q1, Q2, Q3, Q4, Q5]), "radius" : 20 * mm, "tangentPropagation" : true, "allowEdgeOverflow" : false});
        }
        {
            var Q0;
            Q0=qCreatedBy(makeId("Front.planeOp"),FACE);
            var sketch = newSketch(context, id + "F14", { "sketchPlane" : qUnion([Q0])});
            skEllipticalArc(sketch, "E87", {});
            skFitSpline(sketch, "E88", {"points": [v(151.03, -29.08) * mm, v(202.66, 48.48) * mm, v(170, 136.3) * mm, v(209.65, 181.52) * mm, v(269.06, 191.96) * mm, v(314, 190.35) * mm, v(324.44, 179.1) * mm, v(329.26, 129.34) * mm, v(365.38, 115.7) * mm, v(391.05, 124.1) * mm, v(415.76, 121.94) * mm, v(411.99, 87.9) * mm, v(379.83, 49.87) * mm, v(441.98, -43.99) * mm], "startDerivative": vector(956.64, 835.65) * mm, "endDerivative": vector(565.74, -825.83) * mm});
            skCircle(sketch, "E89", {"center": v(289.12, 49.07) * mm, "radius": 50.27 * mm});
            skLineSegment(sketch, "E90.bottom", {"start": v(350.02, -102.42) * mm, "end": v(232.43, -102.42) * mm});
            skLineSegment(sketch, "E90.top", {"start": v(350.02, -126.75) * mm, "end": v(232.43, -126.75) * mm});
            skLineSegment(sketch, "E90.left", {"start": v(350.02, -102.42) * mm, "end": v(350.02, -126.75) * mm});
            skLineSegment(sketch, "E90.right", {"start": v(232.43, -102.42) * mm, "end": v(232.43, -126.75) * mm});
            skFitSpline(sketch, "E91", {"points": [v(251.63, -126.75) * mm, v(266.39, -131.58) * mm, v(269.1, -133.47) * mm, v(310.73, -133.7) * mm, v(314.12, -131.6) * mm, v(329.4, -126.75) * mm], "startDerivative": vector(109.5, 0) * mm, "endDerivative": vector(99.46, 0) * mm});
            const initialGuessF14  = {"E87": [0.2912269169051055, -0.11458753889437895, -1, 0, 0.17119749185595087, 0.14899100738065812, 5.6719151107080386, 3.635259316072852]};
            skSetInitialGuess(sketch, initialGuessF14);
            skSolve(sketch);
        }
        {
            var Q0;
            Q0=makeQuery(id+"F14.imprint","IMPRINT",FACE,{"disambiguationData":[TD([[makeQuery(id+"F14.imprint","IMPRINT",EDGE,{"derivedFrom":sQuery(id+"F14.wireOp",EDGE,"E87")}),1.0]])]});
            var Q1;
            Q1=makeQuery(id+"F14.imprint","IMPRINT",FACE,{"disambiguationData":[TD([[makeQuery(id+"F14.imprint","IMPRINT",EDGE,{"derivedFrom":sQuery(id+"F14.wireOp",EDGE,"E90.bottom")}),1.0]])]});
            var Q2;
            {var subQ0=sQuery(id+"F14.wireOp",EDGE,"E91");Q2=makeQuery(id+"F14.imprint","IMPRINT",FACE,{"disambiguationData":[TD([[makeQuery(id+"F14.imprint","IMPRINT",EDGE,{"derivedFrom":subQ0}),1.0]])]});}
            extrude(context, id + "F15", {"entities" : qUnion([Q0, Q1, Q2]), "depth" : 60 * mm});
        }
        {
            var Q0;
            Q0=makeQuery(id+"F15.opExtrude","CAP_FACE",FACE,{"disambiguationData":[OSD([sQuery(id+"F14.wireOp",EDGE,"E87"),sQuery(id+"F14.wireOp",EDGE,"E88"),sQuery(id+"F14.wireOp",EDGE,"E89")])],"isStart":false});
            var Q1;
            Q1=makeQuery(id+"F15.opExtrude","SWEPT_FACE",FACE,{"disambiguationData":[OSD([sQuery(id+"F14.wireOp",EDGE,"E89")])]});
            var Q2;
            Q2=makeQuery(id+"F15.opExtrude","SWEPT_BODY",BODY,{"disambiguationData":[OSD([sQuery(id+"F14.wireOp",EDGE,"E87"),sQuery(id+"F14.wireOp",EDGE,"E88"),sQuery(id+"F14.wireOp",EDGE,"E89")])]});
            shell(context, id + "F16", {"entities" : qUnion([Q0, Q1]), "parts" : qUnion([Q2]), "thickness" : 2 * mm});
        }
        {
            var Q0;
            Q0=makeQuery(id+"F14.imprint","IMPRINT",FACE,{"disambiguationData":[TD([[makeQuery(id+"F14.imprint","IMPRINT",EDGE,{"derivedFrom":sQuery(id+"F14.wireOp",EDGE,"E89")}),1.0]])]});
            extrude(context, id + "F17", {"entities" : qUnion([Q0]), "operationType" : NewBodyOperationType.ADD, "depth" : 2 * mm});
        }
        {
            var Q0;
            Q0=makeQuery(id+"F15.opExtrude","CAP_FACE",FACE,{"disambiguationData":[OSD([sQuery(id+"F14.wireOp",EDGE,"E87"),sQuery(id+"F14.wireOp",EDGE,"E88"),sQuery(id+"F14.wireOp",EDGE,"E89")])],"isStart":false});
            var sketch = newSketch(context, id + "F18", { "sketchPlane" : qUnion([Q0])});
            skEllipticalArc(sketch, "E92", {});
            skFitSpline(sketch, "E93", {"points": [v(151.03, -29.08) * mm, v(202.64, 48.6) * mm, v(170, 136.12) * mm, v(209.62, 181.5) * mm, v(269.06, 191.96) * mm, v(314.06, 190.34) * mm, v(324.45, 179.09) * mm, v(329.26, 129.34) * mm, v(365.35, 115.69) * mm, v(391.06, 124.1) * mm, v(415.78, 121.92) * mm, v(412.01, 87.93) * mm, v(379.83, 49.84) * mm, v(441.98, -43.99) * mm], "startDerivative": vector(878.14, 737.61) * mm, "endDerivative": vector(719.8, -1072.2) * mm});
            skCircle(sketch, "E94", {"center": v(289.12, 49.07) * mm, "radius": 50.46 * mm});
            skLineSegment(sketch, "E95.bottom", {"start": v(232.2, -101.62) * mm, "end": v(349.95, -101.62) * mm});
            skLineSegment(sketch, "E95.top", {"start": v(232.2, -126.63) * mm, "end": v(349.95, -126.63) * mm});
            skLineSegment(sketch, "E95.left", {"start": v(232.2, -101.62) * mm, "end": v(232.2, -126.63) * mm});
            skLineSegment(sketch, "E95.right", {"start": v(349.95, -101.62) * mm, "end": v(349.95, -126.63) * mm});
            skFitSpline(sketch, "E96", {"points": [v(251.31, -126.63) * mm, v(266.49, -131.97) * mm, v(269.86, -133.65) * mm, v(310.6, -133.65) * mm, v(314.82, -131.12) * mm, v(329.72, -126.63) * mm], "startDerivative": vector(155.52, 0) * mm, "endDerivative": vector(142.33, 0) * mm});
            const initialGuessF18  = {"E92": [0.2912269169051055, -0.11458753889437895, -1, 0, 0.17066155463045873, 0.14901363820743405, 5.662694146117774, 4.449675889087349]};
            skSetInitialGuess(sketch, initialGuessF18);
            skSolve(sketch);
        }
        {
            var Q0;
            Q0=makeQuery(id+"F18.imprint","IMPRINT",FACE,{"disambiguationData":[TD([[makeQuery(id+"F18.imprint","IMPRINT",EDGE,{"derivedFrom":sQuery(id+"F18.wireOp",EDGE,"E94")}),-1.0]])]});
            var Q1;
            Q1=makeQuery(id+"F18.imprint","IMPRINT",FACE,{"disambiguationData":[TD([[makeQuery(id+"F18.imprint","IMPRINT",EDGE,{"derivedFrom":sQuery(id+"F18.wireOp",EDGE,"E95.bottom")}),-1.0]])]});
            var Q2;
            {var subQ0=sQuery(id+"F18.wireOp",EDGE,"E96");Q2=makeQuery(id+"F18.imprint","IMPRINT",FACE,{"disambiguationData":[TD([[makeQuery(id+"F18.imprint","IMPRINT",EDGE,{"derivedFrom":subQ0}),1.0]])]});}
            extrude(context, id + "F19", {"entities" : qUnion([Q0, Q1, Q2]), "operationType" : NewBodyOperationType.ADD, "oppositeDirection" : true, "depth" : 2 * mm});
        }
        {
            var Q0;
            {var subQ0=sQuery(id+"F14.wireOp",EDGE,"E88");var subQ1=sQuery(id+"F14.wireOp",EDGE,"E87");Q0=makeQuery(id+"F19.boolean.opBoolean","MERGE",FACE,{"derivedFrom":[makeQuery(id+"F15.opExtrude","CAP_FACE",FACE,{"disambiguationData":[OSD([subQ1,subQ0,sQuery(id+"F14.wireOp",EDGE,"E89")])],"isStart":false}),makeQuery(id+"F19.opExtrude","CAP_FACE",FACE,{"disambiguationData":[OSD([subQ1,subQ0,sQuery(id+"F18.wireOp",EDGE,"E94")])],"isStart":true})]});}
            var sketch = newSketch(context, id + "F20", { "sketchPlane" : qUnion([Q0])});
            skLineSegment(sketch, "E97.bottom", {"start": v(282.91, 99.15) * mm, "end": v(292.99, 99.15) * mm});
            skLineSegment(sketch, "E97.top", {"start": v(282.91, 192.54) * mm, "end": v(292.99, 192.54) * mm});
            skLineSegment(sketch, "E97.left", {"start": v(282.91, 99.15) * mm, "end": v(282.91, 192.54) * mm});
            skLineSegment(sketch, "E97.right", {"start": v(292.99, 99.15) * mm, "end": v(292.99, 192.54) * mm});
            skSolve(sketch);
        }
        {
            var Q0;
            {var subQ0=sQuery(id+"F20.wireOp",EDGE,"E97.left");var subQ1=sQuery(id+"F20.wireOp",EDGE,"E97.top");var subQ2=makeQuery(id+"F20.imprint","INTERSECT",VERTEX,{"derivedFrom":[subQ1,subQ0]});Q0=makeQuery(id+"F20.imprint","IMPRINT",FACE,{"disambiguationData":[TD([[makeQuery(id+"F20.imprint","IMPRINT",EDGE,{"disambiguationData":[TD([[subQ2,-1.0]])],"derivedFrom":subQ1}),-1.0]])]});}
            var Q1;
            {var subQ0=sQuery(id+"F20.wireOp",EDGE,"E97.bottom");Q1=makeQuery(id+"F20.imprint","IMPRINT",FACE,{"disambiguationData":[TD([[makeQuery(id+"F20.imprint","IMPRINT",EDGE,{"derivedFrom":subQ0}),1.0]])]});}
            var Q2;
            {var subQ1=sQuery(id+"F20.wireOp",EDGE,"E97.top");var subQ2=makeQuery(id+"F15.opExtrude","CAP_EDGE",EDGE,{"disambiguationData":[OSD([sQuery(id+"F14.wireOp",EDGE,"E88")])],"isStart":false});var subQ8=makeQuery(id+"F20.imprint","INTERSECT",VERTEX,{"derivedFrom":[subQ2,subQ1]});Q2=makeQuery(id+"F20.imprint","IMPRINT",FACE,{"disambiguationData":[TD([[makeQuery(id+"F20.imprint","IMPRINT",EDGE,{"disambiguationData":[TD([[subQ8,1.0]])],"derivedFrom":subQ2}),-1.0]])]});}
            extrude(context, id + "F21", {"entities" : qUnion([Q0, Q1, Q2]), "depth" : 0.1 * mm});
        }
    });
